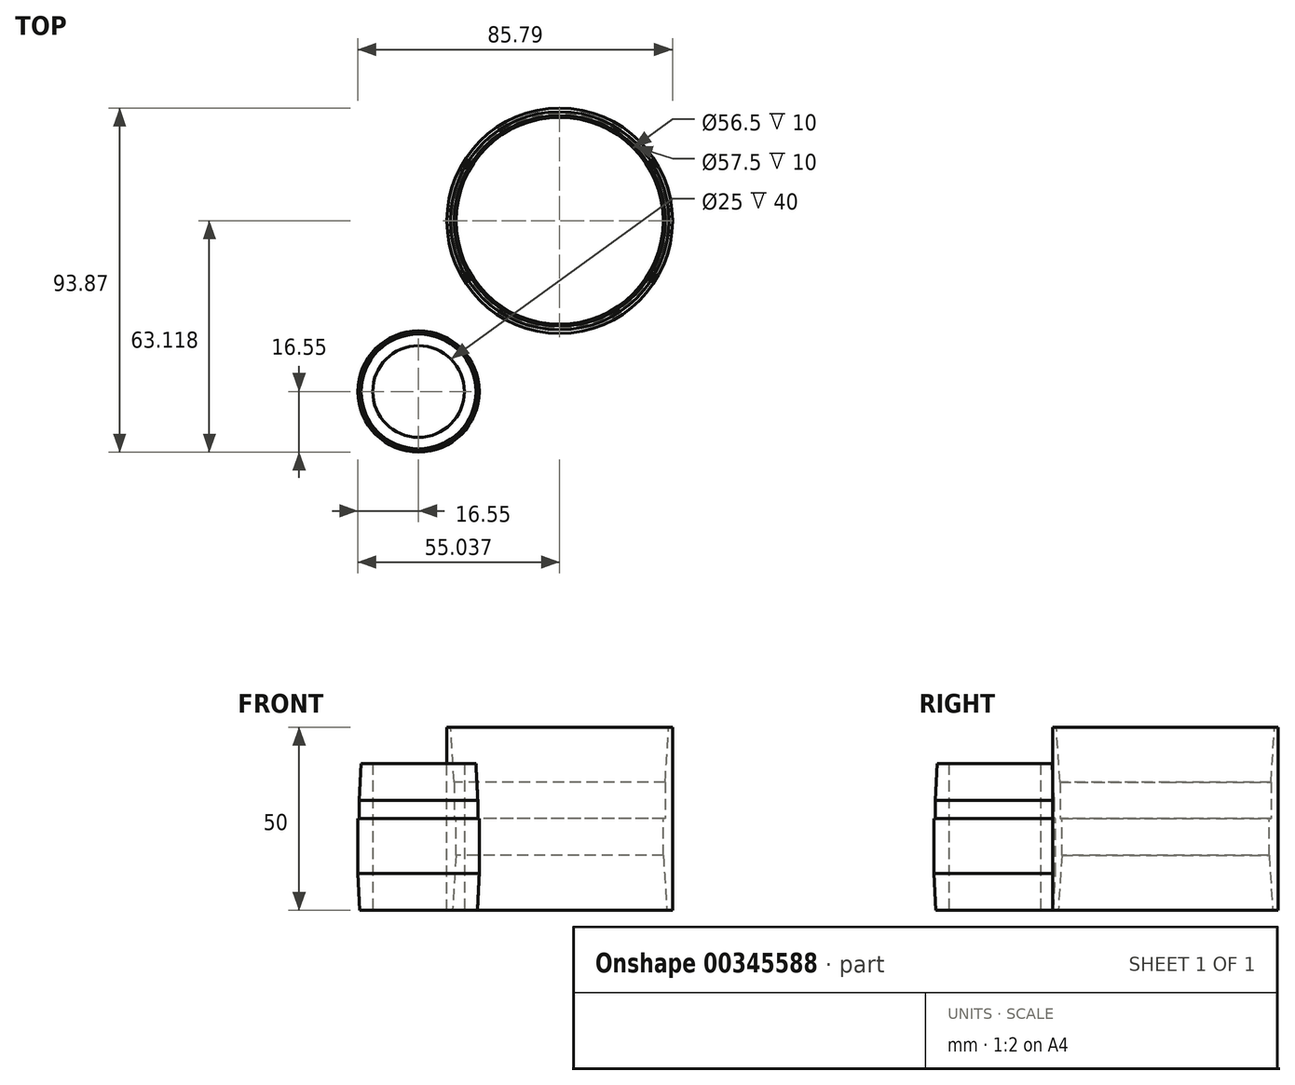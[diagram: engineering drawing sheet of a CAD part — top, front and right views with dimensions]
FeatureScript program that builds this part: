
annotation { "Feature Type Name" : "Feature", "Feature Type Description" : "" }
export const myFeature = defineFeature(function(context is Context, id is Id, definition is map)
    precondition{}
    {
        {
            var Q0;
            Q0=qCreatedBy(makeId("Top.planeOp"),FACE);
            var sketch = newSketch(context, id + "F0", { "sketchPlane" : qUnion([Q0])});
            skCircle(sketch, "E0", {"center": v(0, 0) * mm, "radius": 16.15 * mm});
            skCircle(sketch, "E1", {"center": v(0, 0) * mm, "radius": 12.5 * mm});
            skCircle(sketch, "E2", {"center": v(0, 0) * mm, "radius": 16.55 * mm});
            skSolve(sketch);
        }
        {
            var Q0;
            Q0=makeQuery(id+"F0.imprint","IMPRINT",FACE,{"disambiguationData":[TD([[makeQuery(id+"F0.imprint","IMPRINT",EDGE,{"derivedFrom":sQuery(id+"F0.wireOp",EDGE,"E0")}),1.0]])]});
            extrude(context, id + "F1", {"entities" : qUnion([Q0]), "depth" : 15 * mm});
        }
        {
            var Q0;
            Q0=makeQuery(id+"F0.imprint","IMPRINT",FACE,{"disambiguationData":[TD([[makeQuery(id+"F0.imprint","IMPRINT",EDGE,{"derivedFrom":sQuery(id+"F0.wireOp",EDGE,"E0")}),-1.0]])]});
            var Q1;
            Q1=makeQuery(id+"F0.imprint","IMPRINT",FACE,{"disambiguationData":[TD([[makeQuery(id+"F0.imprint","IMPRINT",EDGE,{"derivedFrom":sQuery(id+"F0.wireOp",EDGE,"E0")}),1.0]])]});
            extrude(context, id + "F2", {"entities" : qUnion([Q0, Q1]), "operationType" : NewBodyOperationType.ADD, "oppositeDirection" : true, "depth" : 25 * mm});
        }
        {
            var Q0;
            Q0=makeQuery(id+"F1.opExtrude","CAP_EDGE",EDGE,{"disambiguationData":[OSD([sQuery(id+"F0.wireOp",EDGE,"E0")])],"isStart":false});
            chamfer(context, id + "F3", {"entities" : qUnion([Q0]), "chamferType" : ChamferType.TWO_OFFSETS, "width1" : .5 * mm, "oppositeDirection" : false, "width2" : 10 * mm, "tangentPropagation" : true});
        }
        {
            var Q0;
            Q0=makeQuery(id+"F2.opExtrude","CAP_EDGE",EDGE,{"disambiguationData":[OSD([sQuery(id+"F0.wireOp",EDGE,"E2")])],"isStart":false});
            chamfer(context, id + "F4", {"entities" : qUnion([Q0]), "chamferType" : ChamferType.TWO_OFFSETS, "width1" : 10 * mm, "oppositeDirection" : false, "width2" : .5 * mm, "tangentPropagation" : true});
        }
        {
            var Q0;
            Q0=qCreatedBy(makeId("Top.planeOp"),FACE);
            var sketch = newSketch(context, id + "F5", { "sketchPlane" : qUnion([Q0])});
            skCircle(sketch, "E3", {"center": v(38.49, 46.57) * mm, "radius": 28.25 * mm});
            skCircle(sketch, "E4", {"center": v(38.49, 46.57) * mm, "radius": 28.75 * mm});
            skCircle(sketch, "E5", {"center": v(38.49, 46.57) * mm, "radius": 30.75 * mm});
            skSolve(sketch);
        }
        {
            var Q0;
            Q0=makeQuery(id+"F5.imprint","IMPRINT",FACE,{"disambiguationData":[TD([[makeQuery(id+"F5.imprint","IMPRINT",EDGE,{"derivedFrom":sQuery(id+"F5.wireOp",EDGE,"E4")}),-1.0]])]});
            var Q1;
            Q1=makeQuery(id+"F5.imprint","IMPRINT",FACE,{"disambiguationData":[TD([[makeQuery(id+"F5.imprint","IMPRINT",EDGE,{"derivedFrom":sQuery(id+"F5.wireOp",EDGE,"E3")}),-1.0]])]});
            extrude(context, id + "F6", {"entities" : qUnion([Q0, Q1]), "oppositeDirection" : true, "depth" : 25 * mm});
        }
        {
            var Q0;
            Q0=makeQuery(id+"F5.imprint","IMPRINT",FACE,{"disambiguationData":[TD([[makeQuery(id+"F5.imprint","IMPRINT",EDGE,{"derivedFrom":sQuery(id+"F5.wireOp",EDGE,"E4")}),-1.0]])]});
            extrude(context, id + "F7", {"entities" : qUnion([Q0]), "operationType" : NewBodyOperationType.ADD, "depth" : 25 * mm});
        }
        {
            var Q0;
            Q0=makeQuery(id+"F7.opExtrude","CAP_EDGE",EDGE,{"disambiguationData":[OSD([sQuery(id+"F5.wireOp",EDGE,"E4")])],"isStart":false});
            chamfer(context, id + "F8", {"entities" : qUnion([Q0]), "chamferType" : ChamferType.TWO_OFFSETS, "width1" : 15 * mm, "oppositeDirection" : false, "width2" : 1 * mm, "tangentPropagation" : true});
        }
        {
            var Q0;
            Q0=makeQuery(id+"F6.opExtrude","CAP_EDGE",EDGE,{"disambiguationData":[OSD([sQuery(id+"F5.wireOp",EDGE,"E3")])],"isStart":false});
            chamfer(context, id + "F9", {"entities" : qUnion([Q0]), "chamferType" : ChamferType.TWO_OFFSETS, "width1" : 1 * mm, "oppositeDirection" : false, "width2" : 15 * mm, "tangentPropagation" : true});
        }
    });
